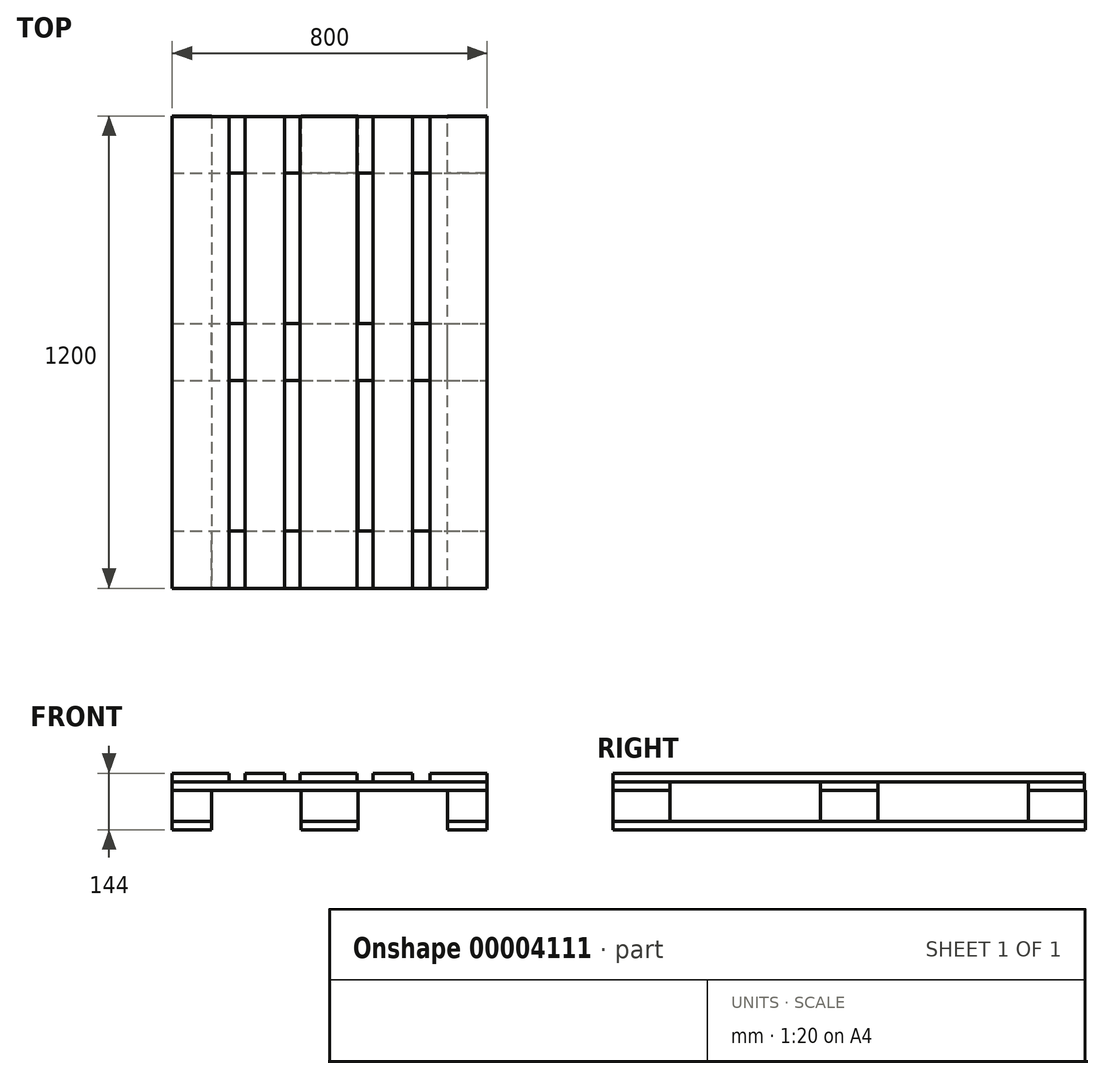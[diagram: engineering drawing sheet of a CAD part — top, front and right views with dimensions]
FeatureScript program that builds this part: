
annotation { "Feature Type Name" : "Feature", "Feature Type Description" : "" }
export const myFeature = defineFeature(function(context is Context, id is Id, definition is map)
    precondition{}
    {
        {
            var Q0;
            Q0=qCreatedBy(makeId("Top.planeOp"),FACE);
            var sketch = newSketch(context, id + "F0", { "sketchPlane" : qUnion([Q0])});
            skLineSegment(sketch, "E0.bottom", {"start": v(-100, 600) * mm, "end": v(0, 600) * mm});
            skLineSegment(sketch, "E0.top", {"start": v(-100, -600) * mm, "end": v(0, -600) * mm});
            skLineSegment(sketch, "E0.left", {"start": v(-100, 600) * mm, "end": v(-100, -600) * mm});
            skLineSegment(sketch, "E0.right", {"start": v(0, 600) * mm, "end": v(0, -600) * mm});
            skLineSegment(sketch, "E1.bottom", {"start": v(227.5, -600) * mm, "end": v(372.5, -600) * mm});
            skLineSegment(sketch, "E1.top", {"start": v(227.5, 600) * mm, "end": v(372.5, 600) * mm});
            skLineSegment(sketch, "E1.left", {"start": v(227.5, -600) * mm, "end": v(227.5, 600) * mm});
            skLineSegment(sketch, "E1.right", {"start": v(372.5, -600) * mm, "end": v(372.5, 600) * mm});
            skPoint(sketch, "E2", {"position": v(300, -600) * mm});
            skLineSegment(sketch, "E3.bottom", {"start": v(600, -600) * mm, "end": v(700, -600) * mm});
            skLineSegment(sketch, "E3.top", {"start": v(600, 600) * mm, "end": v(700, 600) * mm});
            skLineSegment(sketch, "E3.left", {"start": v(600, -600) * mm, "end": v(600, 600) * mm});
            skLineSegment(sketch, "E3.right", {"start": v(700, -600) * mm, "end": v(700, 600) * mm});
            skSolve(sketch);
        }
        {
            var Q0;
            Q0 = qSketchRegion(id + "F0", true);
            extrude(context, id + "F1", {"entities" : qUnion([Q0]), "depth" : 22 * mm});
        }
        {
            var Q0;
            Q0=makeQuery(id+"F1.opExtrude","CAP_FACE",FACE,{"disambiguationData":[OSD([sQuery(id+"F0.wireOp",EDGE,"E3.bottom"),sQuery(id+"F0.wireOp",EDGE,"E3.top"),sQuery(id+"F0.wireOp",EDGE,"E3.left"),sQuery(id+"F0.wireOp",EDGE,"E3.right")])],"isStart":false});
            var sketch = newSketch(context, id + "F2", { "sketchPlane" : qUnion([Q0])});
            skLineSegment(sketch, "E4.bottom", {"start": v(-100, -600) * mm, "end": v(0, -600) * mm});
            skLineSegment(sketch, "E4.top", {"start": v(-100, -455) * mm, "end": v(0, -455) * mm});
            skLineSegment(sketch, "E4.left", {"start": v(-100, -600) * mm, "end": v(-100, -455) * mm});
            skLineSegment(sketch, "E4.right", {"start": v(0, -600) * mm, "end": v(0, -455) * mm});
            skLineSegment(sketch, "E5.bottom", {"start": v(227.5, -600) * mm, "end": v(372.5, -600) * mm});
            skLineSegment(sketch, "E5.top", {"start": v(227.5, -455) * mm, "end": v(372.5, -455) * mm});
            skLineSegment(sketch, "E5.left", {"start": v(227.5, -600) * mm, "end": v(227.5, -455) * mm});
            skLineSegment(sketch, "E5.right", {"start": v(372.5, -600) * mm, "end": v(372.5, -455) * mm});
            skLineSegment(sketch, "E6.bottom", {"start": v(600, -600) * mm, "end": v(700, -600) * mm});
            skLineSegment(sketch, "E6.top", {"start": v(600, -455) * mm, "end": v(700, -455) * mm});
            skLineSegment(sketch, "E6.left", {"start": v(600, -600) * mm, "end": v(600, -455) * mm});
            skLineSegment(sketch, "E6.right", {"start": v(700, -600) * mm, "end": v(700, -455) * mm});
            skLineSegment(sketch, "E7.bottom", {"start": v(700, 600) * mm, "end": v(600, 600) * mm});
            skLineSegment(sketch, "E7.top", {"start": v(700, 455) * mm, "end": v(600, 455) * mm});
            skLineSegment(sketch, "E7.left", {"start": v(700, 600) * mm, "end": v(700, 455) * mm});
            skLineSegment(sketch, "E7.right", {"start": v(600, 600) * mm, "end": v(600, 455) * mm});
            skLineSegment(sketch, "E8.bottom", {"start": v(372.5, 600) * mm, "end": v(227.5, 600) * mm});
            skLineSegment(sketch, "E8.top", {"start": v(372.5, 455) * mm, "end": v(227.5, 455) * mm});
            skLineSegment(sketch, "E8.left", {"start": v(372.5, 600) * mm, "end": v(372.5, 455) * mm});
            skLineSegment(sketch, "E8.right", {"start": v(227.5, 600) * mm, "end": v(227.5, 455) * mm});
            skLineSegment(sketch, "E9.bottom", {"start": v(-100, 600) * mm, "end": v(0, 600) * mm});
            skLineSegment(sketch, "E9.top", {"start": v(-100, 455) * mm, "end": v(0, 455) * mm});
            skLineSegment(sketch, "E9.left", {"start": v(-100, 600) * mm, "end": v(-100, 455) * mm});
            skLineSegment(sketch, "E9.right", {"start": v(0, 600) * mm, "end": v(0, 455) * mm});
            skLineSegment(sketch, "E10.bottom", {"start": v(-100, -72.5) * mm, "end": v(0, -72.5) * mm});
            skLineSegment(sketch, "E10.top", {"start": v(-100, 72.5) * mm, "end": v(0, 72.5) * mm});
            skLineSegment(sketch, "E10.left", {"start": v(-100, -72.5) * mm, "end": v(-100, 72.5) * mm});
            skLineSegment(sketch, "E10.right", {"start": v(0, -72.5) * mm, "end": v(0, 72.5) * mm});
            skLineSegment(sketch, "E11.bottom", {"start": v(227.5, -72.5) * mm, "end": v(372.5, -72.5) * mm});
            skLineSegment(sketch, "E11.top", {"start": v(227.5, 72.5) * mm, "end": v(372.5, 72.5) * mm});
            skLineSegment(sketch, "E11.left", {"start": v(227.5, -72.5) * mm, "end": v(227.5, 72.5) * mm});
            skLineSegment(sketch, "E11.right", {"start": v(372.5, -72.5) * mm, "end": v(372.5, 72.5) * mm});
            skLineSegment(sketch, "E12.bottom", {"start": v(600, -72.5) * mm, "end": v(700, -72.5) * mm});
            skLineSegment(sketch, "E12.top", {"start": v(600, 72.5) * mm, "end": v(700, 72.5) * mm});
            skLineSegment(sketch, "E12.left", {"start": v(600, -72.5) * mm, "end": v(600, 72.5) * mm});
            skLineSegment(sketch, "E12.right", {"start": v(700, -72.5) * mm, "end": v(700, 72.5) * mm});
            skSolve(sketch);
        }
        {
            var Q0;
            Q0=makeQuery(id+"F2.imprint","IMPRINT",FACE,{"disambiguationData":[TD([[makeQuery(id+"F2.imprint","IMPRINT",EDGE,{"derivedFrom":sQuery(id+"F2.wireOp",EDGE,"E4.bottom")}),1.0]])]});
            var Q1;
            Q1=makeQuery(id+"F2.imprint","IMPRINT",FACE,{"disambiguationData":[TD([[makeQuery(id+"F2.imprint","IMPRINT",EDGE,{"derivedFrom":sQuery(id+"F2.wireOp",EDGE,"E5.bottom")}),1.0]])]});
            var Q2;
            Q2=makeQuery(id+"F2.imprint","IMPRINT",FACE,{"disambiguationData":[TD([[makeQuery(id+"F2.imprint","IMPRINT",EDGE,{"derivedFrom":sQuery(id+"F2.wireOp",EDGE,"E6.bottom")}),1.0]])]});
            var Q3;
            Q3=makeQuery(id+"F2.imprint","IMPRINT",FACE,{"disambiguationData":[TD([[makeQuery(id+"F2.imprint","IMPRINT",EDGE,{"derivedFrom":sQuery(id+"F2.wireOp",EDGE,"E7.bottom")}),1.0]])]});
            var Q4;
            Q4=makeQuery(id+"F2.imprint","IMPRINT",FACE,{"disambiguationData":[TD([[makeQuery(id+"F2.imprint","IMPRINT",EDGE,{"derivedFrom":sQuery(id+"F2.wireOp",EDGE,"E8.bottom")}),1.0]])]});
            var Q5;
            Q5=makeQuery(id+"F2.imprint","IMPRINT",FACE,{"disambiguationData":[TD([[makeQuery(id+"F2.imprint","IMPRINT",EDGE,{"derivedFrom":sQuery(id+"F2.wireOp",EDGE,"E9.bottom")}),-1.0]])]});
            var Q6;
            Q6=makeQuery(id+"F2.imprint","IMPRINT",FACE,{"disambiguationData":[TD([[makeQuery(id+"F2.imprint","IMPRINT",EDGE,{"derivedFrom":sQuery(id+"F2.wireOp",EDGE,"E10.bottom")}),1.0]])]});
            var Q7;
            Q7=makeQuery(id+"F2.imprint","IMPRINT",FACE,{"disambiguationData":[TD([[makeQuery(id+"F2.imprint","IMPRINT",EDGE,{"derivedFrom":sQuery(id+"F2.wireOp",EDGE,"E11.bottom")}),1.0]])]});
            var Q8;
            Q8=makeQuery(id+"F2.imprint","IMPRINT",FACE,{"disambiguationData":[TD([[makeQuery(id+"F2.imprint","IMPRINT",EDGE,{"derivedFrom":sQuery(id+"F2.wireOp",EDGE,"E12.bottom")}),1.0]])]});
            var Q9;
            Q9=makeQuery(id+"F2.imprint","IMPRINT",FACE,{"disambiguationData":[TD([[makeQuery(id+"F2.imprint","IMPRINT",EDGE,{"derivedFrom":sQuery(id+"F2.wireOp",EDGE,"E7.bottom")}),-1.0]])]});
            extrude(context, id + "F3", {"entities" : qUnion([Q0, Q1, Q2, Q3, Q4, Q5, Q6, Q7, Q8, Q9]), "depth" : 78 * mm});
        }
        {
            var Q0;
            Q0=makeQuery(id+"F3.opExtrude","CAP_FACE",FACE,{"disambiguationData":[OSD([sQuery(id+"F2.wireOp",EDGE,"E9.bottom"),sQuery(id+"F2.wireOp",EDGE,"E9.top"),sQuery(id+"F2.wireOp",EDGE,"E9.left"),sQuery(id+"F2.wireOp",EDGE,"E9.right")])],"isStart":false});
            var sketch = newSketch(context, id + "F4", { "sketchPlane" : qUnion([Q0])});
            skLineSegment(sketch, "E13.bottom", {"start": v(-100, -600) * mm, "end": v(700, -600) * mm});
            skLineSegment(sketch, "E13.top", {"start": v(-100, -455) * mm, "end": v(700, -455) * mm});
            skLineSegment(sketch, "E13.left", {"start": v(-100, -600) * mm, "end": v(-100, -455) * mm});
            skLineSegment(sketch, "E13.right", {"start": v(700, -600) * mm, "end": v(700, -455) * mm});
            skLineSegment(sketch, "E14.bottom", {"start": v(-100, -72.5) * mm, "end": v(700, -72.5) * mm});
            skLineSegment(sketch, "E14.top", {"start": v(-100, 72.5) * mm, "end": v(700, 72.5) * mm});
            skLineSegment(sketch, "E14.left", {"start": v(-100, -72.5) * mm, "end": v(-100, 72.5) * mm});
            skLineSegment(sketch, "E14.right", {"start": v(700, -72.5) * mm, "end": v(700, 72.5) * mm});
            skLineSegment(sketch, "E15.bottom", {"start": v(-100, 455) * mm, "end": v(700, 455) * mm});
            skLineSegment(sketch, "E15.top", {"start": v(-100, 597.77) * mm, "end": v(700, 597.77) * mm});
            skLineSegment(sketch, "E15.left", {"start": v(-100, 455) * mm, "end": v(-100, 597.77) * mm});
            skLineSegment(sketch, "E15.right", {"start": v(700, 455) * mm, "end": v(700, 597.77) * mm});
            skSolve(sketch);
        }
        {
            var Q0;
            Q0=makeQuery(id+"F4.imprint","IMPRINT",FACE,{"disambiguationData":[TD([[makeQuery(id+"F4.imprint","IMPRINT",EDGE,{"derivedFrom":sQuery(id+"F4.wireOp",EDGE,"E13.bottom")}),1.0]])]});
            var Q1;
            Q1=makeQuery(id+"F4.imprint","IMPRINT",FACE,{"disambiguationData":[TD([[makeQuery(id+"F4.imprint","IMPRINT",EDGE,{"derivedFrom":sQuery(id+"F4.wireOp",EDGE,"E14.bottom")}),1.0]])]});
            var Q2;
            {var subQ5=sQuery(id+"F4.wireOp",EDGE,"E15.left");Q2=makeQuery(id+"F4.imprint","IMPRINT",FACE,{"disambiguationData":[TD([[makeQuery(id+"F4.imprint","IMPRINT",EDGE,{"derivedFrom":subQ5}),1.0]])]});}
            var Q3;
            {var subQ5=sQuery(id+"F4.wireOp",EDGE,"E15.right");Q3=makeQuery(id+"F4.imprint","IMPRINT",FACE,{"disambiguationData":[TD([[makeQuery(id+"F4.imprint","IMPRINT",EDGE,{"derivedFrom":subQ5}),1.0]])]});}
            extrude(context, id + "F5", {"entities" : qUnion([Q0, Q1, Q2, Q3]), "depth" : 22 * mm});
        }
        {
            var Q0;
            Q0=makeQuery(id+"F5.opExtrude","CAP_FACE",FACE,{"disambiguationData":[OSD([sQuery(id+"F4.wireOp",EDGE,"E13.bottom"),sQuery(id+"F4.wireOp",EDGE,"E13.top"),sQuery(id+"F4.wireOp",EDGE,"E13.left"),sQuery(id+"F4.wireOp",EDGE,"E13.right")])],"isStart":false});
            var sketch = newSketch(context, id + "F6", { "sketchPlane" : qUnion([Q0])});
            skLineSegment(sketch, "E16.bottom", {"start": v(-100, -600) * mm, "end": v(45, -600) * mm});
            skLineSegment(sketch, "E16.top", {"start": v(-100, 597.77) * mm, "end": v(45, 597.77) * mm});
            skLineSegment(sketch, "E16.left", {"start": v(-100, -600) * mm, "end": v(-100, 597.77) * mm});
            skLineSegment(sketch, "E16.right", {"start": v(45, -600) * mm, "end": v(45, 597.77) * mm});
            skLineSegment(sketch, "E17.bottom", {"start": v(700, 597.77) * mm, "end": v(555, 597.77) * mm});
            skLineSegment(sketch, "E17.top", {"start": v(700, -600) * mm, "end": v(555, -600) * mm});
            skLineSegment(sketch, "E17.left", {"start": v(700, 597.77) * mm, "end": v(700, -600) * mm});
            skLineSegment(sketch, "E17.right", {"start": v(555, 597.77) * mm, "end": v(555, -600) * mm});
            skLineSegment(sketch, "E18.bottom", {"start": v(510, -600) * mm, "end": v(410, -600) * mm});
            skLineSegment(sketch, "E18.top", {"start": v(510, 597.77) * mm, "end": v(410, 597.77) * mm});
            skLineSegment(sketch, "E18.left", {"start": v(510, -600) * mm, "end": v(510, 597.77) * mm});
            skLineSegment(sketch, "E18.right", {"start": v(410, -600) * mm, "end": v(410, 597.77) * mm});
            skLineSegment(sketch, "E19.bottom", {"start": v(370, -600) * mm, "end": v(225, -600) * mm});
            skLineSegment(sketch, "E19.top", {"start": v(370, 597.77) * mm, "end": v(225, 597.77) * mm});
            skLineSegment(sketch, "E19.left", {"start": v(370, -600) * mm, "end": v(370, 597.77) * mm});
            skLineSegment(sketch, "E19.right", {"start": v(225, -600) * mm, "end": v(225, 597.77) * mm});
            skLineSegment(sketch, "E20.bottom", {"start": v(185, -600) * mm, "end": v(85, -600) * mm});
            skLineSegment(sketch, "E20.top", {"start": v(185, 597.77) * mm, "end": v(85, 597.77) * mm});
            skLineSegment(sketch, "E20.left", {"start": v(185, -600) * mm, "end": v(185, 597.77) * mm});
            skLineSegment(sketch, "E20.right", {"start": v(85, -600) * mm, "end": v(85, 597.77) * mm});
            skSolve(sketch);
        }
        {
            var Q0;
            {var subQ5=sQuery(id+"F6.wireOp",EDGE,"E16.bottom");Q0=makeQuery(id+"F6.imprint","IMPRINT",FACE,{"disambiguationData":[TD([[makeQuery(id+"F6.imprint","IMPRINT",EDGE,{"derivedFrom":subQ5}),1.0]])]});}
            var Q1;
            {var subQ5=sQuery(id+"F6.wireOp",EDGE,"E16.top");Q1=makeQuery(id+"F6.imprint","IMPRINT",FACE,{"disambiguationData":[TD([[makeQuery(id+"F6.imprint","IMPRINT",EDGE,{"derivedFrom":subQ5}),-1.0]])]});}
            var Q2;
            {var subQ6=sQuery(id+"F6.wireOp",EDGE,"E20.bottom");Q2=makeQuery(id+"F6.imprint","IMPRINT",FACE,{"disambiguationData":[TD([[makeQuery(id+"F6.imprint","IMPRINT",EDGE,{"derivedFrom":subQ6}),1.0]])]});}
            var Q3;
            {var subQ5=sQuery(id+"F6.wireOp",EDGE,"E20.top");Q3=makeQuery(id+"F6.imprint","IMPRINT",FACE,{"disambiguationData":[TD([[makeQuery(id+"F6.imprint","IMPRINT",EDGE,{"derivedFrom":subQ5}),1.0]])]});}
            var Q4;
            {var subQ6=sQuery(id+"F6.wireOp",EDGE,"E19.bottom");Q4=makeQuery(id+"F6.imprint","IMPRINT",FACE,{"disambiguationData":[TD([[makeQuery(id+"F6.imprint","IMPRINT",EDGE,{"derivedFrom":subQ6}),1.0]])]});}
            var Q5;
            {var subQ5=sQuery(id+"F6.wireOp",EDGE,"E19.top");Q5=makeQuery(id+"F6.imprint","IMPRINT",FACE,{"disambiguationData":[TD([[makeQuery(id+"F6.imprint","IMPRINT",EDGE,{"derivedFrom":subQ5}),1.0]])]});}
            var Q6;
            {var subQ5=sQuery(id+"F6.wireOp",EDGE,"E18.top");Q6=makeQuery(id+"F6.imprint","IMPRINT",FACE,{"disambiguationData":[TD([[makeQuery(id+"F6.imprint","IMPRINT",EDGE,{"derivedFrom":subQ5}),1.0]])]});}
            var Q7;
            {var subQ5=sQuery(id+"F6.wireOp",EDGE,"E17.top");Q7=makeQuery(id+"F6.imprint","IMPRINT",FACE,{"disambiguationData":[TD([[makeQuery(id+"F6.imprint","IMPRINT",EDGE,{"derivedFrom":subQ5}),1.0]])]});}
            var Q8;
            {var subQ5=sQuery(id+"F6.wireOp",EDGE,"E17.bottom");Q8=makeQuery(id+"F6.imprint","IMPRINT",FACE,{"disambiguationData":[TD([[makeQuery(id+"F6.imprint","IMPRINT",EDGE,{"derivedFrom":subQ5}),1.0]])]});}
            var Q9;
            {var subQ6=sQuery(id+"F6.wireOp",EDGE,"E18.bottom");Q9=makeQuery(id+"F6.imprint","IMPRINT",FACE,{"disambiguationData":[TD([[makeQuery(id+"F6.imprint","IMPRINT",EDGE,{"derivedFrom":subQ6}),1.0]])]});}
            extrude(context, id + "F7", {"entities" : qUnion([Q0, Q1, Q2, Q3, Q4, Q5, Q6, Q7, Q8, Q9]), "depth" : 22 * mm});
        }
    });
